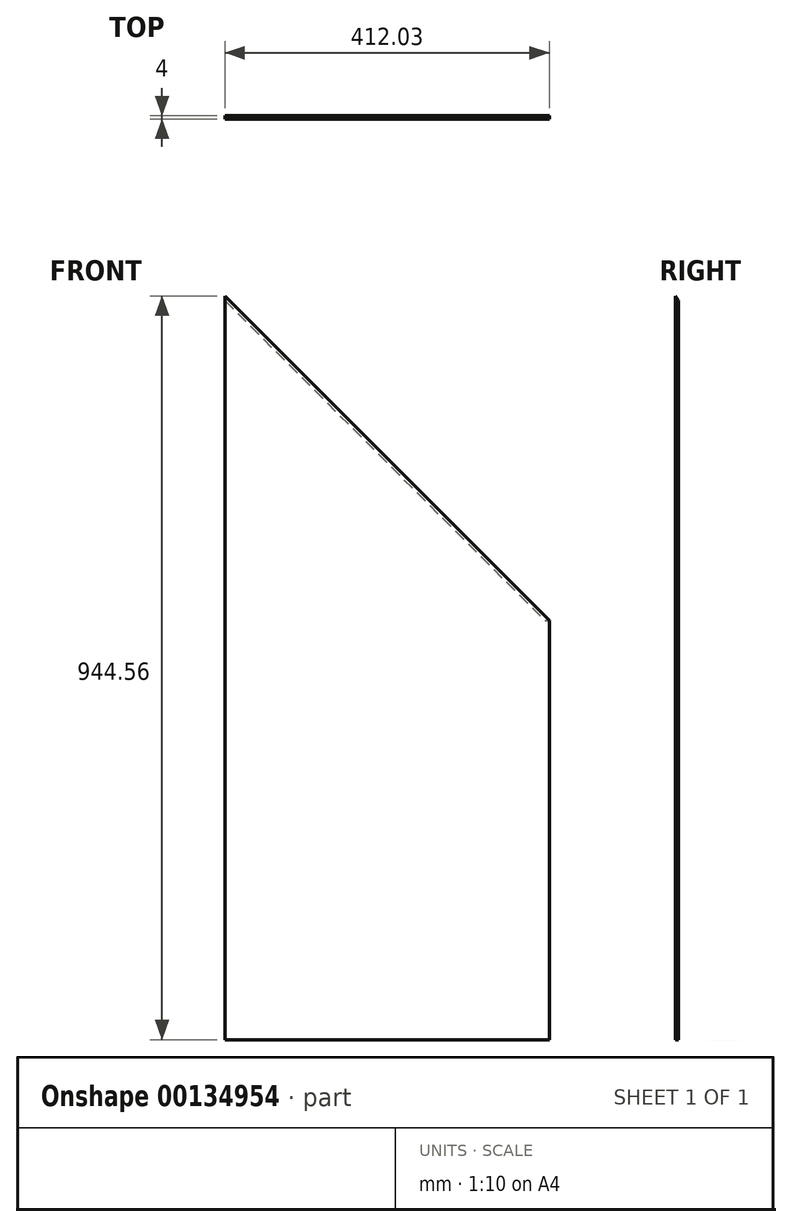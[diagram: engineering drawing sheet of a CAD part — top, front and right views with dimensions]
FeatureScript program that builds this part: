
annotation { "Feature Type Name" : "Feature", "Feature Type Description" : "" }
export const myFeature = defineFeature(function(context is Context, id is Id, definition is map)
    precondition{}
    {
        {
            var Q0;
            Q0=qCreatedBy(makeId("Front.planeOp"),FACE);
            var sketch = newSketch(context, id + "F0", { "sketchPlane" : qUnion([Q0])});
            skLineSegment(sketch, "E0", {"start": v(0, 0) * mm, "end": v(412.03, 0) * mm});
            skLineSegment(sketch, "E1", {"start": v(412.03, 0) * mm, "end": v(412.03, 532.53) * mm});
            skLineSegment(sketch, "E2", {"start": v(412.03, 532.53) * mm, "end": v(0, 944.56) * mm});
            skLineSegment(sketch, "E3", {"start": v(0, 944.56) * mm, "end": v(0, 0) * mm});
            skSolve(sketch);
        }
        {
            var Q0;
            Q0=makeQuery(id+"F0.imprint","IMPRINT",FACE,{"disambiguationData":[TD([[makeQuery(id+"F0.imprint","IMPRINT",EDGE,{"derivedFrom":sQuery(id+"F0.wireOp",EDGE,"E0")}),1.0]])]});
            extrude(context, id + "F1", {"entities" : qUnion([Q0]), "depth" : 4 * mm});
        }
        {
            var Q0;
            Q0=makeQuery(id+"F1.opExtrude","CAP_EDGE",EDGE,{"disambiguationData":[OSD([sQuery(id+"F0.wireOp",EDGE,"E2")])],"isStart":true});
            chamfer(context, id + "F2", {"entities" : qUnion([Q0]), "width" : 4 * mm, "tangentPropagation" : true});
        }
        {
            var Q0;
            Q0=makeQuery(id+"F1.opExtrude","SWEPT_FACE",FACE,{"disambiguationData":[OSD([sQuery(id+"F0.wireOp",EDGE,"E1")])]});
            var sketch = newSketch(context, id + "F3", { "sketchPlane" : qUnion([Q0])});
            skLineSegment(sketch, "E4.bottom", {"start": v(0, 526.87) * mm, "end": v(-4, 526.87) * mm});
            skLineSegment(sketch, "E4.top", {"start": v(0, 532.53) * mm, "end": v(-4, 532.53) * mm});
            skLineSegment(sketch, "E4.left", {"start": v(0, 526.87) * mm, "end": v(0, 532.53) * mm});
            skLineSegment(sketch, "E4.right", {"start": v(-4, 526.87) * mm, "end": v(-4, 532.53) * mm});
            skSolve(sketch);
        }
        {
            var Q0;
            Q0=makeQuery(id+"F3.imprint","IMPRINT",FACE,{"disambiguationData":[TD([[makeQuery(id+"F3.imprint","IMPRINT",EDGE,{"derivedFrom":sQuery(id+"F3.wireOp",EDGE,"E4.top")}),1.0]])]});
            extrude(context, id + "F4", {"entities" : qUnion([Q0]), "operationType" : NewBodyOperationType.ADD, "oppositeDirection" : true, "depth" : 25 * mm});
        }
    });
